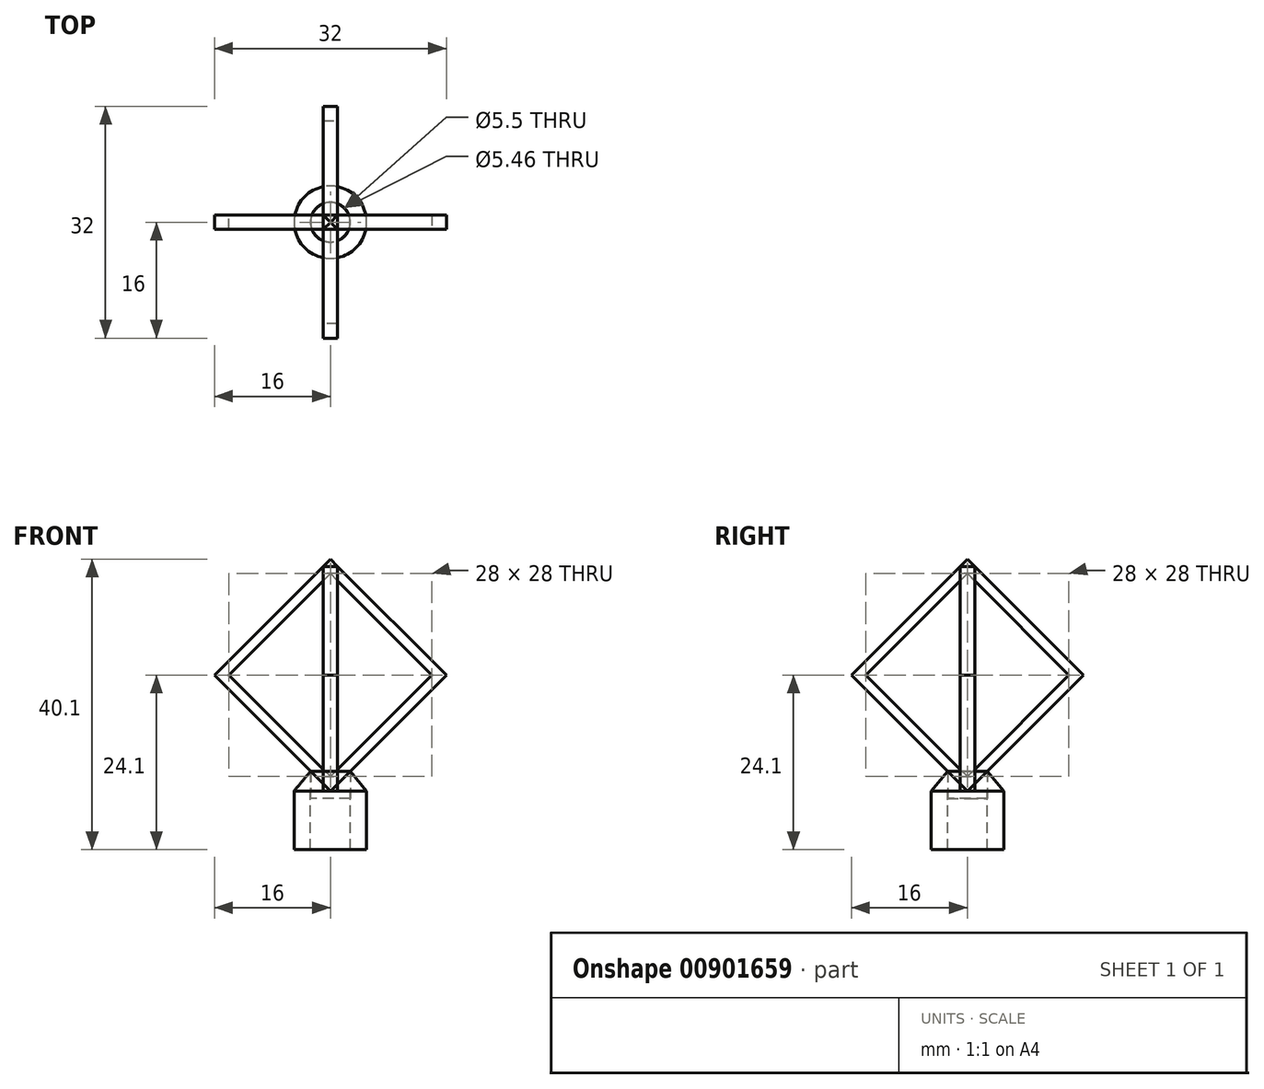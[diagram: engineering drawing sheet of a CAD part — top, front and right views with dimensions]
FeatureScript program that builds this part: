
annotation { "Feature Type Name" : "Feature", "Feature Type Description" : "" }
export const myFeature = defineFeature(function(context is Context, id is Id, definition is map)
    precondition{}
    {
        {
            var Q0;
            Q0=qCreatedBy(makeId("Front.planeOp"),FACE);
            var sketch = newSketch(context, id + "F0", { "sketchPlane" : qUnion([Q0])});
            skLineSegment(sketch, "E0", {"start": v(0, 15) * mm, "end": v(0, -15) * mm});
            skLineSegment(sketch, "E1", {"start": v(-15, 0) * mm, "end": v(15, 0) * mm});
            skLineSegment(sketch, "E2", {"start": v(0, -15) * mm, "end": v(-15, 0) * mm});
            skLineSegment(sketch, "E3", {"start": v(-15, 0) * mm, "end": v(0, 15) * mm});
            skLineSegment(sketch, "E4", {"start": v(0, 15) * mm, "end": v(15, 0) * mm});
            skLineSegment(sketch, "E5", {"start": v(15, 0) * mm, "end": v(0, -15) * mm});
            skSolve(sketch);
        }
        {
            var Q0;
            Q0=sQuery(id+"F0.wireOp",EDGE,"E0");
            cPlane(context, id + "F1", {"entities" : qUnion([Q0]), "cplaneType" : CPlaneType.LINE_ANGLE, "offset" : 25 * mm, "angle" : 0 * degree, "width" : 150 * mm, "height" : 150 * mm});
        }
        {
            var Q0;
            Q0=qCreatedBy(id+"F1.planeOp",FACE);
            var sketch = newSketch(context, id + "F2", { "sketchPlane" : qUnion([Q0])});
            skLineSegment(sketch, "E6.bottom", {"start": v(-1, 16) * mm, "end": v(1, 16) * mm});
            skLineSegment(sketch, "E6.top", {"start": v(-1, 14) * mm, "end": v(1, 14) * mm});
            skLineSegment(sketch, "E6.left", {"start": v(-1, 16) * mm, "end": v(-1, 14) * mm});
            skLineSegment(sketch, "E6.right", {"start": v(1, 16) * mm, "end": v(1, 14) * mm});
            skPoint(sketch, "E7", {"position": v(0, 14) * mm});
            skSolve(sketch);
        }
        {
            var Q0;
            Q0=makeQuery(id+"F2.imprint","IMPRINT",FACE,{"disambiguationData":[TD([[makeQuery(id+"F2.imprint","IMPRINT",EDGE,{"derivedFrom":sQuery(id+"F2.wireOp",EDGE,"E6.bottom")}),-1.0]])]});
            var Q1;
            Q1=sQuery(id+"F0.wireOp",EDGE,"E3");
            var Q2;
            Q2=sQuery(id+"F0.wireOp",EDGE,"E2");
            var Q3;
            Q3=sQuery(id+"F0.wireOp",EDGE,"E5");
            var Q4;
            Q4=sQuery(id+"F0.wireOp",EDGE,"E4");
            sweep(context, id + "F3", {"profiles" : qUnion([Q0]), "path" : qUnion([Q1, Q2, Q3, Q4])});
        }
        {
            var Q0;
            Q0=sQuery(id+"F0.wireOp",EDGE,"E1");
            cPlane(context, id + "F4", {"entities" : qUnion([Q0]), "cplaneType" : CPlaneType.LINE_ANGLE, "offset" : 25 * mm, "angle" : 0 * degree, "width" : 150 * mm, "height" : 150 * mm});
        }
        {
            var Q0;
            Q0=qCreatedBy(id+"F1.planeOp",FACE);
            var sketch = newSketch(context, id + "F5", { "sketchPlane" : qUnion([Q0])});
            skLineSegment(sketch, "E8", {"start": v(-15, 0) * mm, "end": v(15, 0) * mm});
            skLineSegment(sketch, "E9", {"start": v(0, -15) * mm, "end": v(0, 15) * mm});
            skLineSegment(sketch, "E10", {"start": v(0, 15) * mm, "end": v(15, 0) * mm});
            skLineSegment(sketch, "E11", {"start": v(15, 0) * mm, "end": v(0, -15) * mm});
            skLineSegment(sketch, "E12", {"start": v(0, -15) * mm, "end": v(-15, 0) * mm});
            skLineSegment(sketch, "E13", {"start": v(-15, 0) * mm, "end": v(0, 15) * mm});
            skSolve(sketch);
        }
        {
            var Q0;
            Q0=qCreatedBy(id+"F4.planeOp",FACE);
            var sketch = newSketch(context, id + "F6", { "sketchPlane" : qUnion([Q0])});
            skLineSegment(sketch, "E14.bottom", {"start": v(-1, 14) * mm, "end": v(1, 14) * mm});
            skLineSegment(sketch, "E14.top", {"start": v(-1, 16) * mm, "end": v(1, 16) * mm});
            skLineSegment(sketch, "E14.left", {"start": v(-1, 14) * mm, "end": v(-1, 16) * mm});
            skLineSegment(sketch, "E14.right", {"start": v(1, 14) * mm, "end": v(1, 16) * mm});
            skSolve(sketch);
        }
        {
            var Q0;
            Q0=makeQuery(id+"F6.imprint","IMPRINT",FACE,{"disambiguationData":[TD([[makeQuery(id+"F6.imprint","IMPRINT",EDGE,{"derivedFrom":sQuery(id+"F6.wireOp",EDGE,"E14.bottom")}),1.0]])]});
            var Q1;
            Q1=sQuery(id+"F5.wireOp",EDGE,"E13");
            var Q2;
            Q2=sQuery(id+"F5.wireOp",EDGE,"E12");
            var Q3;
            Q3=sQuery(id+"F5.wireOp",EDGE,"E11");
            var Q4;
            Q4=sQuery(id+"F5.wireOp",EDGE,"E10");
            sweep(context, id + "F7", {"profiles" : qUnion([Q0]), "path" : qUnion([Q1, Q2, Q3, Q4])});
        }
        {
            var Q0;
            Q0=makeQuery(id+"F7.opSweep","MID_CAP_VERTEX",VERTEX,{"disambiguationData":[OSD([sQuery(id+"F5.wireOp",EDGE,"E12"),sQuery(id+"F6.wireOp",EDGE,"E14.top"),sQuery(id+"F6.wireOp",EDGE,"E14.left")])],"capPos":2.0});
            var Q1;
            Q1=makeQuery(id+"F7.opSweep","MID_CAP_VERTEX",VERTEX,{"disambiguationData":[OSD([sQuery(id+"F5.wireOp",EDGE,"E12"),sQuery(id+"F6.wireOp",EDGE,"E14.top"),sQuery(id+"F6.wireOp",EDGE,"E14.right")])],"capPos":2.0});
            var Q2;
            Q2=makeQuery(id+"F3.opSweep","MID_CAP_VERTEX",VERTEX,{"disambiguationData":[OSD([sQuery(id+"F0.wireOp",EDGE,"E2"),sQuery(id+"F2.wireOp",EDGE,"E6.bottom"),sQuery(id+"F2.wireOp",EDGE,"E6.left")])],"capPos":2.0});
            cPlane(context, id + "F8", {"entities" : qUnion([Q0, Q1, Q2]), "cplaneType" : CPlaneType.THREE_POINT, "offset" : 25 * mm, "width" : 150 * mm, "height" : 150 * mm});
        }
        {
            var Q0;
            Q0=qCreatedBy(id+"F8.planeOp",FACE);
            var sketch = newSketch(context, id + "F9", { "sketchPlane" : qUnion([Q0])});
            skCircle(sketch, "E15", {"center": v(0, 0) * mm, "radius": 2.75 * mm});
            skCircle(sketch, "E16", {"center": v(0, 0) * mm, "radius": 5 * mm});
            skSolve(sketch);
        }
        {
            var Q0;
            Q0=makeQuery(id+"F9.imprint","IMPRINT",FACE,{"disambiguationData":[TD([[makeQuery(id+"F9.imprint","IMPRINT",EDGE,{"derivedFrom":sQuery(id+"F9.wireOp",EDGE,"E15")}),1.0]])]});
            var Q1;
            Q1=sQuery(id+"F9.wireOp",EDGE,"E15");
            extrude(context, id + "F10", {"entities" : qUnion([Q0]), "surfaceEntities" : qUnion([Q1]), "depth" : 2.73 * mm, "offsetDistance" : 25 * mm, "hasSecondDirection" : true, "secondDirectionOppositeDirection" : true, "secondDirectionDepth" : 1 * mm});
        }
        {
            var Q0;
            Q0=makeQuery(id+"F9.imprint","IMPRINT",FACE,{"disambiguationData":[TD([[makeQuery(id+"F9.imprint","IMPRINT",EDGE,{"derivedFrom":sQuery(id+"F9.wireOp",EDGE,"E15")}),-1.0]])]});
            extrude(context, id + "F11", {"entities" : qUnion([Q0]), "oppositeDirection" : true, "depth" : 8.1 * mm, "offsetDistance" : 25 * mm});
        }
        {
            var Q0;
            Q0=makeQuery(id+"F7.opSweep","SWEPT_FACE",FACE,{"disambiguationData":[OSD([sQuery(id+"F5.wireOp",EDGE,"E13"),sQuery(id+"F6.wireOp",EDGE,"E14.top")])]});
            extrude(context, id + "F12", {"entities" : qUnion([Q0]), "operationType" : NewBodyOperationType.REMOVE, "depth" : 1.7 * mm, "offsetDistance" : 25 * mm});
        }
        {
            var Q0;
            Q0=makeQuery(id+"F7.opSweep","SWEPT_FACE",FACE,{"disambiguationData":[OSD([sQuery(id+"F5.wireOp",EDGE,"E10"),sQuery(id+"F6.wireOp",EDGE,"E14.top")])]});
            extrude(context, id + "F13", {"entities" : qUnion([Q0]), "operationType" : NewBodyOperationType.REMOVE, "depth" : 1.9 * mm, "offsetDistance" : 25 * mm});
        }
        {
            var Q0;
            Q0=makeQuery(id+"F3.opSweep","SWEPT_FACE",FACE,{"disambiguationData":[OSD([sQuery(id+"F0.wireOp",EDGE,"E3"),sQuery(id+"F2.wireOp",EDGE,"E6.bottom")])]});
            extrude(context, id + "F14", {"entities" : qUnion([Q0]), "operationType" : NewBodyOperationType.REMOVE, "depth" : 2.5 * mm, "offsetDistance" : 25 * mm});
        }
        {
            var Q0;
            Q0=makeQuery(id+"F3.opSweep","SWEPT_FACE",FACE,{"disambiguationData":[OSD([sQuery(id+"F0.wireOp",EDGE,"E4"),sQuery(id+"F2.wireOp",EDGE,"E6.bottom")])]});
            extrude(context, id + "F15", {"entities" : qUnion([Q0]), "operationType" : NewBodyOperationType.REMOVE, "depth" : 1.4 * mm, "offsetDistance" : 25 * mm});
        }
        {
            var Q0;
            Q0=qCreatedBy(makeId("Front.planeOp"),FACE);
            var sketch = newSketch(context, id + "F16", { "sketchPlane" : qUnion([Q0])});
            skLineSegment(sketch, "E17", {"start": v(5, -16) * mm, "end": v(2.73, -13.27) * mm});
            skLineSegment(sketch, "E18", {"start": v(2.73, -13.27) * mm, "end": v(2.73, -16) * mm});
            skLineSegment(sketch, "E19", {"start": v(2.73, -16) * mm, "end": v(5, -16) * mm});
            skPoint(sketch, "E20", {"position": v(5, -16) * mm});
            skLineSegment(sketch, "E21", {"start": v(0, -16.04) * mm, "end": v(0, -1.26) * mm});
            skSolve(sketch);
        }
        {
            var Q0;
            Q0=makeQuery(id+"F16.imprint","IMPRINT",FACE,{"disambiguationData":[TD([[makeQuery(id+"F16.imprint","IMPRINT",EDGE,{"derivedFrom":sQuery(id+"F16.wireOp",EDGE,"E17")}),1.0]])]});
            var Q1;
            Q1=sQuery(id+"F16.wireOp",EDGE,"E21");
            revolve(context, id + "F17", {"surfaceOperationType" : NewSurfaceOperationType.NEW, "entities" : qUnion([Q0]), "axis" : qUnion([Q1]), "revolveType" : RevolveType.FULL});
        }
    });
